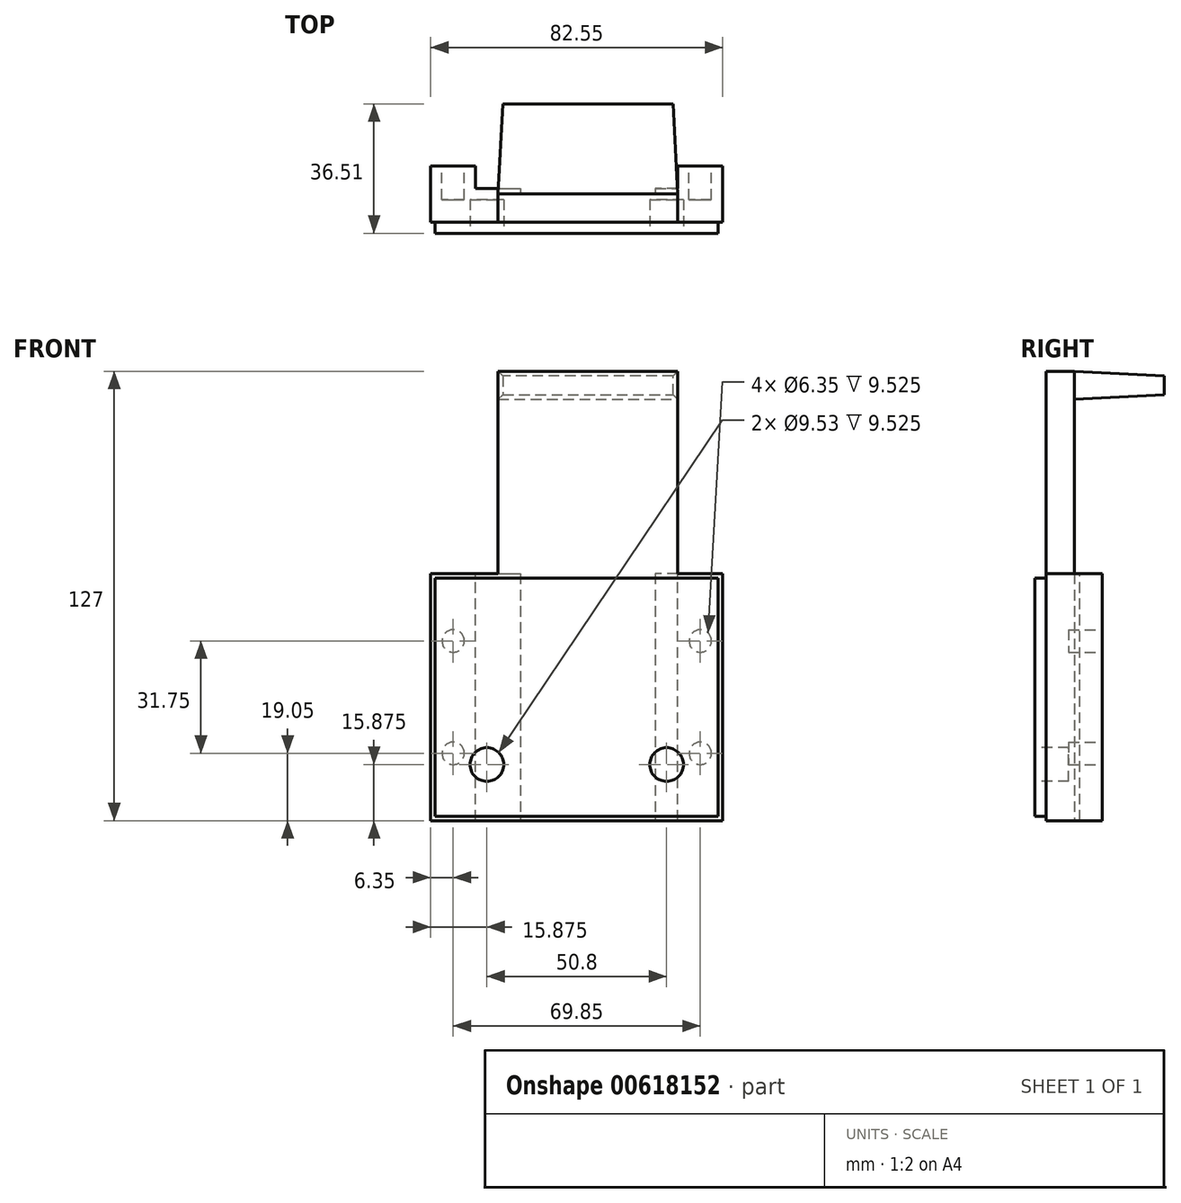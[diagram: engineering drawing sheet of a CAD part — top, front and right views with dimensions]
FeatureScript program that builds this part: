
annotation { "Feature Type Name" : "Feature", "Feature Type Description" : "" }
export const myFeature = defineFeature(function(context is Context, id is Id, definition is map)
    precondition{}
    {
        {
            var Q0;
            Q0=qCreatedBy(makeId("Front.planeOp"),FACE);
            var sketch = newSketch(context, id + "F0", { "sketchPlane" : qUnion([Q0])});
            skLineSegment(sketch, "E0.bottom", {"start": v(0, 0) * mm, "end": v(82.55, 0) * mm});
            skLineSegment(sketch, "E0.top", {"start": v(0, 69.85) * mm, "end": v(82.55, 69.85) * mm});
            skLineSegment(sketch, "E0.left", {"start": v(0, 0) * mm, "end": v(0, 69.85) * mm});
            skLineSegment(sketch, "E0.right", {"start": v(82.55, 0) * mm, "end": v(82.55, 69.85) * mm});
            skLineSegment(sketch, "E1.bottom", {"start": v(19.05, 69.85) * mm, "end": v(69.85, 69.85) * mm});
            skLineSegment(sketch, "E1.top", {"start": v(19.05, 127) * mm, "end": v(69.85, 127) * mm});
            skLineSegment(sketch, "E1.left", {"start": v(19.05, 69.85) * mm, "end": v(19.05, 127) * mm});
            skLineSegment(sketch, "E1.right", {"start": v(69.85, 69.85) * mm, "end": v(69.85, 127) * mm});
            skSolve(sketch);
        }
        {
            var Q0;
            Q0=qSketchRegion(id+"F0",true);
            extrude(context, id + "F1", {"entities" : qUnion([Q0]), "depth" : 7.94 * mm});
        }
        {
            var Q0;
            Q0=makeQuery(id+"F1.opExtrude","CAP_FACE",FACE,{"disambiguationData":[OSD([sQuery(id+"F0.wireOp",EDGE,"E0.bottom"),sQuery(id+"F0.wireOp",EDGE,"E0.top"),sQuery(id+"F0.wireOp",EDGE,"E0.left"),sQuery(id+"F0.wireOp",EDGE,"E0.right"),sQuery(id+"F0.wireOp",EDGE,"E1.top"),sQuery(id+"F0.wireOp",EDGE,"E1.left"),sQuery(id+"F0.wireOp",EDGE,"E1.right")])],"isStart":true});
            var sketch = newSketch(context, id + "F2", { "sketchPlane" : qUnion([Q0])});
            skLineSegment(sketch, "E2.bottom", {"start": v(0, 0) * mm, "end": v(-12.7, 0) * mm});
            skLineSegment(sketch, "E2.top", {"start": v(0, 69.85) * mm, "end": v(-12.7, 69.85) * mm});
            skLineSegment(sketch, "E2.left", {"start": v(0, 0) * mm, "end": v(0, 69.85) * mm});
            skLineSegment(sketch, "E2.right", {"start": v(-12.7, 0) * mm, "end": v(-12.7, 69.85) * mm});
            skLineSegment(sketch, "E3.bottom", {"start": v(-82.55, 0) * mm, "end": v(-69.85, 0) * mm});
            skLineSegment(sketch, "E3.top", {"start": v(-82.55, 69.85) * mm, "end": v(-69.85, 69.85) * mm});
            skLineSegment(sketch, "E3.left", {"start": v(-82.55, 0) * mm, "end": v(-82.55, 69.85) * mm});
            skLineSegment(sketch, "E3.right", {"start": v(-69.85, 0) * mm, "end": v(-69.85, 69.85) * mm});
            skSolve(sketch);
        }
        {
            var Q0;
            Q0=qSketchRegion(id+"F2",true);
            extrude(context, id + "F3", {"entities" : qUnion([Q0]), "operationType" : NewBodyOperationType.ADD, "depth" : 7.94 * mm});
        }
        {
            var Q0;
            Q0=makeQuery(id+"F1.opExtrude","CAP_FACE",FACE,{"disambiguationData":[OSD([sQuery(id+"F0.wireOp",EDGE,"E0.bottom"),sQuery(id+"F0.wireOp",EDGE,"E0.top"),sQuery(id+"F0.wireOp",EDGE,"E0.left"),sQuery(id+"F0.wireOp",EDGE,"E0.right"),sQuery(id+"F0.wireOp",EDGE,"E1.top"),sQuery(id+"F0.wireOp",EDGE,"E1.left"),sQuery(id+"F0.wireOp",EDGE,"E1.right")])],"isStart":true});
            var sketch = newSketch(context, id + "F4", { "sketchPlane" : qUnion([Q0])});
            skLineSegment(sketch, "E4.bottom", {"start": v(-12.7, 69.85) * mm, "end": v(-25.4, 69.85) * mm});
            skLineSegment(sketch, "E4.top", {"start": v(-12.7, 0) * mm, "end": v(-25.4, 0) * mm});
            skLineSegment(sketch, "E4.left", {"start": v(-12.7, 69.85) * mm, "end": v(-12.7, 0) * mm});
            skLineSegment(sketch, "E4.right", {"start": v(-25.4, 69.85) * mm, "end": v(-25.4, 0) * mm});
            skLineSegment(sketch, "E5.bottom", {"start": v(-69.85, 69.85) * mm, "end": v(-63.5, 69.85) * mm});
            skLineSegment(sketch, "E5.top", {"start": v(-69.85, 0) * mm, "end": v(-63.5, 0) * mm});
            skLineSegment(sketch, "E5.left", {"start": v(-69.85, 69.85) * mm, "end": v(-69.85, 0) * mm});
            skLineSegment(sketch, "E5.right", {"start": v(-63.5, 69.85) * mm, "end": v(-63.5, 0) * mm});
            skSolve(sketch);
        }
        {
            var Q0;
            Q0=qSketchRegion(id+"F4",true);
            extrude(context, id + "F5", {"entities" : qUnion([Q0]), "operationType" : NewBodyOperationType.ADD, "depth" : 1.59 * mm});
        }
        {
            var Q0;
            Q0=makeQuery(id+"F1.opExtrude","CAP_FACE",FACE,{"disambiguationData":[OSD([sQuery(id+"F0.wireOp",EDGE,"E0.bottom"),sQuery(id+"F0.wireOp",EDGE,"E0.top"),sQuery(id+"F0.wireOp",EDGE,"E0.left"),sQuery(id+"F0.wireOp",EDGE,"E0.right"),sQuery(id+"F0.wireOp",EDGE,"E1.top"),sQuery(id+"F0.wireOp",EDGE,"E1.left"),sQuery(id+"F0.wireOp",EDGE,"E1.right")])],"isStart":true});
            var sketch = newSketch(context, id + "F6", { "sketchPlane" : qUnion([Q0])});
            skLineSegment(sketch, "E6.bottom", {"start": v(-69.85, 127) * mm, "end": v(-19.05, 127) * mm});
            skLineSegment(sketch, "E6.top", {"start": v(-69.85, 119.06) * mm, "end": v(-19.05, 119.06) * mm});
            skLineSegment(sketch, "E6.left", {"start": v(-69.85, 127) * mm, "end": v(-69.85, 119.06) * mm});
            skLineSegment(sketch, "E6.right", {"start": v(-19.05, 127) * mm, "end": v(-19.05, 119.06) * mm});
            skSolve(sketch);
        }
        {
            var Q0;
            Q0=qSketchRegion(id+"F6",true);
            extrude(context, id + "F7", {"entities" : qUnion([Q0]), "operationType" : NewBodyOperationType.ADD, "depth" : 25.4 * mm, "hasDraft" : true, "draftAngle" : 3 * degree, "draftPullDirection" : true});
        }
        {
            var Q0;
            Q0=makeQuery(id+"F1.opExtrude","CAP_FACE",FACE,{"disambiguationData":[OSD([sQuery(id+"F0.wireOp",EDGE,"E0.bottom"),sQuery(id+"F0.wireOp",EDGE,"E0.top"),sQuery(id+"F0.wireOp",EDGE,"E0.left"),sQuery(id+"F0.wireOp",EDGE,"E0.right"),sQuery(id+"F0.wireOp",EDGE,"E1.top"),sQuery(id+"F0.wireOp",EDGE,"E1.left"),sQuery(id+"F0.wireOp",EDGE,"E1.right")])],"isStart":false});
            var sketch = newSketch(context, id + "F8", { "sketchPlane" : qUnion([Q0])});
            skLineSegment(sketch, "E7.bottom", {"start": v(0, 69.85) * mm, "end": v(82.55, 69.85) * mm});
            skLineSegment(sketch, "E7.top", {"start": v(0, 0) * mm, "end": v(82.55, 0) * mm});
            skLineSegment(sketch, "E7.left", {"start": v(0, 69.85) * mm, "end": v(0, 0) * mm});
            skLineSegment(sketch, "E7.right", {"start": v(82.55, 69.85) * mm, "end": v(82.55, 0) * mm});
            skLineSegment(sketch, "E8.0", {"start": v(1.27, 68.58) * mm, "end": v(1.27, 1.27) * mm});
            skLineSegment(sketch, "E8.1", {"start": v(1.27, 68.58) * mm, "end": v(81.28, 68.58) * mm});
            skLineSegment(sketch, "E8.2", {"start": v(81.28, 68.58) * mm, "end": v(81.28, 1.27) * mm});
            skLineSegment(sketch, "E8.3", {"start": v(1.27, 1.27) * mm, "end": v(81.28, 1.27) * mm});
            skSolve(sketch);
        }
        {
            var Q0;
            Q0=makeQuery(id+"F8.imprint","IMPRINT",FACE,{"disambiguationData":[TD([[makeQuery(id+"F8.imprint","IMPRINT",EDGE,{"derivedFrom":sQuery(id+"F8.wireOp",EDGE,"E8.0")}),1.0]])]});
            extrude(context, id + "F9", {"entities" : qUnion([Q0]), "operationType" : NewBodyOperationType.ADD, "depth" : 3.17 * mm});
        }
        {
            var Q0;
            Q0=makeQuery(id+"F9.opExtrude","CAP_FACE",FACE,{"disambiguationData":[OSD([sQuery(id+"F8.wireOp",EDGE,"E8.0"),sQuery(id+"F8.wireOp",EDGE,"E8.1"),sQuery(id+"F8.wireOp",EDGE,"E8.2"),sQuery(id+"F8.wireOp",EDGE,"E8.3")])],"isStart":false});
            var sketch = newSketch(context, id + "F10", { "sketchPlane" : qUnion([Q0])});
            skCircle(sketch, "E9", {"center": v(15.88, 15.88) * mm, "radius": 4.76 * mm});
            skCircle(sketch, "E10", {"center": v(66.68, 15.88) * mm, "radius": 4.76 * mm});
            skSolve(sketch);
        }
        {
            var Q0;
            Q0=qSketchRegion(id+"F10",true);
            extrude(context, id + "F11", {"entities" : qUnion([Q0]), "operationType" : NewBodyOperationType.REMOVE, "oppositeDirection" : true, "depth" : 9.52 * mm});
        }
        {
            var Q0;
            Q0=makeQuery(id+"F3.opExtrude","CAP_FACE",FACE,{"disambiguationData":[OSD([sQuery(id+"F2.wireOp",EDGE,"E3.bottom"),sQuery(id+"F2.wireOp",EDGE,"E3.top"),sQuery(id+"F2.wireOp",EDGE,"E3.left"),sQuery(id+"F2.wireOp",EDGE,"E3.right")])],"isStart":false});
            var sketch = newSketch(context, id + "F12", { "sketchPlane" : qUnion([Q0])});
            skCircle(sketch, "E11", {"center": v(-76.2, 50.8) * mm, "radius": 3.18 * mm});
            skCircle(sketch, "E12", {"center": v(-76.2, 19.05) * mm, "radius": 3.18 * mm});
            skCircle(sketch, "E13", {"center": v(-6.35, 50.8) * mm, "radius": 3.18 * mm});
            skCircle(sketch, "E14", {"center": v(-6.35, 19.05) * mm, "radius": 3.18 * mm});
            skSolve(sketch);
        }
        {
            var Q0;
            Q0=qSketchRegion(id+"F12",true);
            extrude(context, id + "F13", {"entities" : qUnion([Q0]), "operationType" : NewBodyOperationType.REMOVE, "oppositeDirection" : true, "depth" : 9.52 * mm});
        }
    });
